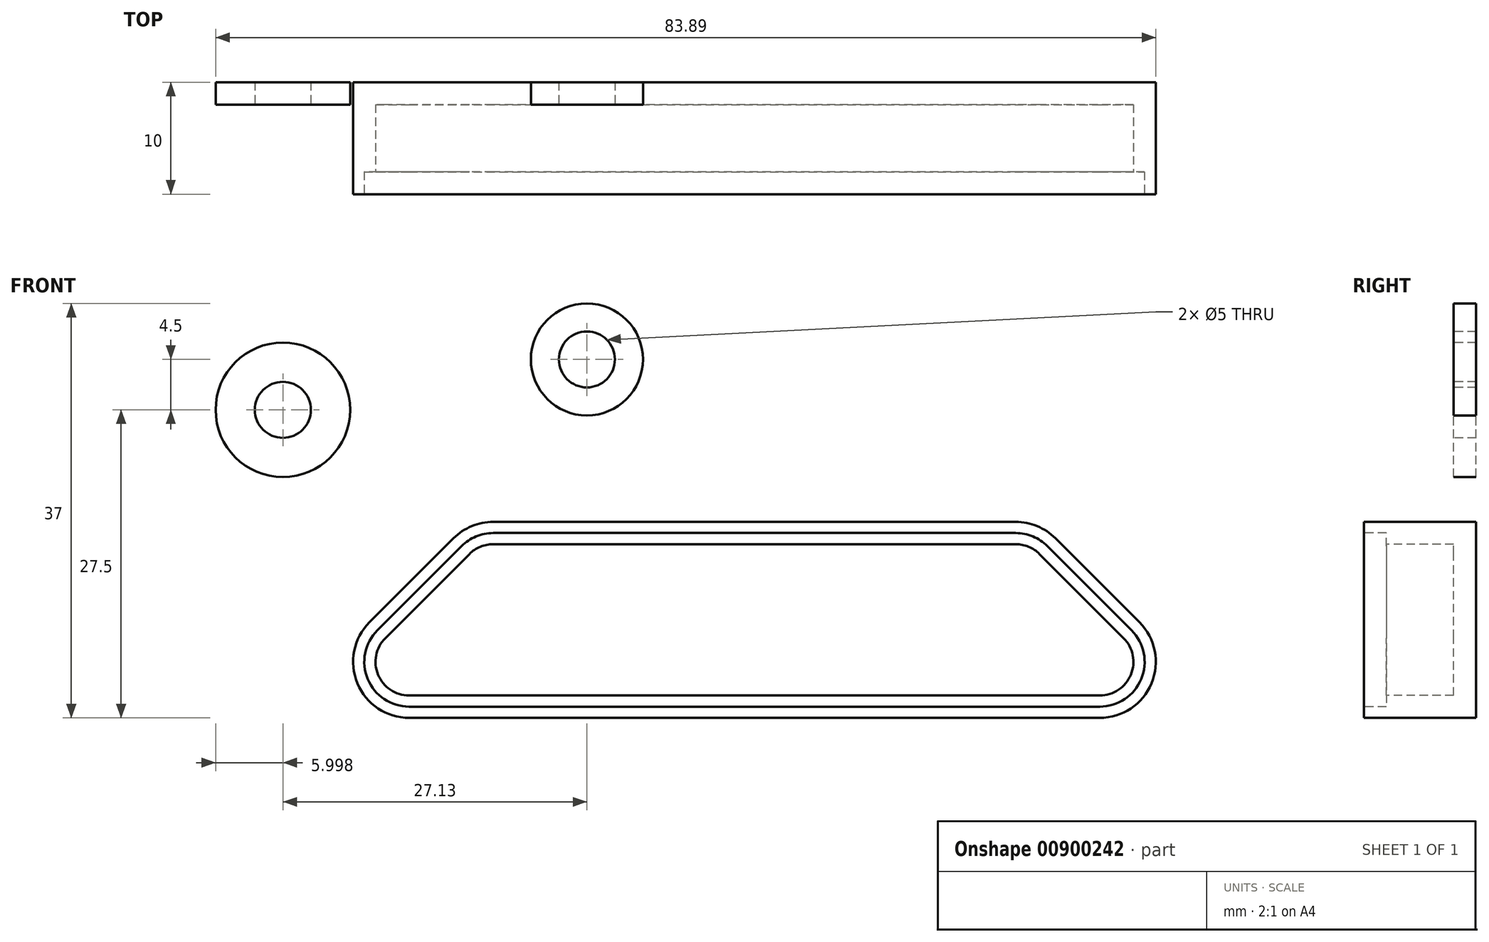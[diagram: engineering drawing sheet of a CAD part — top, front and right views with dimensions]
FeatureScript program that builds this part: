
annotation { "Feature Type Name" : "Feature", "Feature Type Description" : "" }
export const myFeature = defineFeature(function(context is Context, id is Id, definition is map)
    precondition{}
    {
        {
            var Q0;
            Q0=qCreatedBy(makeId("Front.planeOp"),FACE);
            var sketch = newSketch(context, id + "F0", { "sketchPlane" : qUnion([Q0])});
            skLineSegment(sketch, "E0", {"start": v(-36.08, 0) * mm, "end": v(36.08, 0) * mm, "construction": true});
            skArc(sketch, "E1", {"start": v(36.08, -20) * mm, "mid": v(56.08, 0) * mm, "end": v(36.08, 20) * mm});
            skArc(sketch, "E2", {"start": v(-36.08, 20) * mm, "mid": v(-56.08, 0) * mm, "end": v(-36.08, -20) * mm});
            skLineSegment(sketch, "E3", {"start": v(-36.08, 20) * mm, "end": v(36.08, 20) * mm});
            skLineSegment(sketch, "E4.MirrorCS", {"start": v(-36.08, -20) * mm, "end": v(36.08, -20) * mm});
            skSolve(sketch);
        }
        {
            var Q0;
            Q0 = qSketchRegion(id + "F0", true);
            extrude(context, id + "F1", {"entities" : qUnion([Q0]), "depth" : 2 * mm, "offsetDistance" : 25 * mm});
        }
        {
            var Q0;
            Q0=makeQuery(id+"F1.opExtrude","CAP_FACE",FACE,{"disambiguationData":[OSD([sQuery(id+"F0.wireOp",EDGE,"E1"),sQuery(id+"F0.wireOp",EDGE,"E2"),sQuery(id+"F0.wireOp",EDGE,"E3"),sQuery(id+"F0.wireOp",EDGE,"E4.MirrorCS")])],"isStart":false});
            var sketch = newSketch(context, id + "F2", { "sketchPlane" : qUnion([Q0])});
            skLineSegment(sketch, "E5", {"start": v(0, 107.5) * mm, "end": v(0, -106.96) * mm, "construction": true});
            skLineSegment(sketch, "E6", {"start": v(0, -2.5) * mm, "end": v(23.31, -2.5) * mm});
            skLineSegment(sketch, "E7", {"start": v(26.85, -3.96) * mm, "end": v(34.35, -11.46) * mm});
            skLineSegment(sketch, "E8", {"start": v(30.81, -20) * mm, "end": v(0, -20) * mm});
            skArc(sketch, "E9.filletArc", {"start": v(26.85, -3.96) * mm, "mid": v(25.23, -2.88) * mm, "end": v(23.31, -2.5) * mm});
            skArc(sketch, "E10.filletArc", {"start": v(30.81, -20) * mm, "mid": v(35.43, -16.91) * mm, "end": v(34.35, -11.46) * mm});
            skLineSegment(sketch, "E11.MirrorCS", {"start": v(0, -2.5) * mm, "end": v(-23.31, -2.5) * mm});
            skArc(sketch, "E12.MirrorCS", {"start": v(-26.85, -3.96) * mm, "mid": v(-25.23, -2.88) * mm, "end": v(-23.31, -2.5) * mm});
            skLineSegment(sketch, "E13.MirrorCS", {"start": v(-26.85, -3.96) * mm, "end": v(-34.35, -11.46) * mm});
            skArc(sketch, "E14.MirrorCS", {"start": v(-30.81, -20) * mm, "mid": v(-35.43, -16.91) * mm, "end": v(-34.35, -11.46) * mm});
            skLineSegment(sketch, "E15.MirrorCS", {"start": v(-30.81, -20) * mm, "end": v(0, -20) * mm});
            skSolve(sketch);
        }
        {
            var Q0;
            Q0=makeQuery(id+"F2.imprint","IMPRINT",FACE,{"disambiguationData":[TD([[makeQuery(id+"F2.imprint","IMPRINT",EDGE,{"derivedFrom":sQuery(id+"F2.wireOp",EDGE,"E6")}),-1.0]])]});
            var Q1;
            Q1=makeQuery(id+"F2.imprint","IMPRINT",FACE,{"disambiguationData":[TD([[makeQuery(id+"F2.imprint","IMPRINT",EDGE,{"derivedFrom":sQuery(id+"F2.wireOp",EDGE,"1ff64fa8-2fd5-4123-b6a7-406101e30ad4.0")}),1.0]])]});
            var Q2;
            Q2=makeQuery(id+"F2.imprint","IMPRINT",FACE,{"disambiguationData":[TD([[makeQuery(id+"F2.imprint","IMPRINT",EDGE,{"derivedFrom":sQuery(id+"F2.wireOp",EDGE,"6d2cac0a-8418-49f5-aced-8188614ca164.0")}),1.0]])]});
            extrude(context, id + "F3", {"entities" : qUnion([Q0, Q1, Q2]), "operationType" : NewBodyOperationType.ADD, "depth" : 8 * mm, "offsetDistance" : 25 * mm});
        }
        {
            var Q0;
            Q0=makeQuery(id+"F3.opExtrude","CAP_FACE",FACE,{"disambiguationData":[OSD([sQuery(id+"F2.wireOp",EDGE,"E6"),sQuery(id+"F2.wireOp",EDGE,"E7"),sQuery(id+"F2.wireOp",EDGE,"E8"),sQuery(id+"F2.wireOp",EDGE,"E9.filletArc"),sQuery(id+"F2.wireOp",EDGE,"E10.filletArc"),sQuery(id+"F2.wireOp",EDGE,"E11.MirrorCS"),sQuery(id+"F2.wireOp",EDGE,"E12.MirrorCS"),sQuery(id+"F2.wireOp",EDGE,"E13.MirrorCS"),sQuery(id+"F2.wireOp",EDGE,"E14.MirrorCS"),sQuery(id+"F2.wireOp",EDGE,"E15.MirrorCS")])],"isStart":false});
            var sketch = newSketch(context, id + "F4", { "sketchPlane" : qUnion([Q0])});
            skArc(sketch, "E16.0", {"start": v(-33.64, -12.17) * mm, "mid": v(-34.51, -16.53) * mm, "end": v(-30.81, -19) * mm});
            skLineSegment(sketch, "E16.1", {"start": v(-26.14, -4.67) * mm, "end": v(-33.64, -12.17) * mm});
            skLineSegment(sketch, "E16.2", {"start": v(-30.81, -19) * mm, "end": v(30.81, -19) * mm});
            skArc(sketch, "E16.3", {"start": v(-23.31, -3.5) * mm, "mid": v(-24.85, -3.8) * mm, "end": v(-26.14, -4.67) * mm});
            skArc(sketch, "E16.4", {"start": v(30.81, -19) * mm, "mid": v(34.51, -16.53) * mm, "end": v(33.64, -12.17) * mm});
            skLineSegment(sketch, "E16.5", {"start": v(33.64, -12.17) * mm, "end": v(26.14, -4.67) * mm});
            skArc(sketch, "E16.6", {"start": v(26.14, -4.67) * mm, "mid": v(24.85, -3.8) * mm, "end": v(23.31, -3.5) * mm});
            skLineSegment(sketch, "E16.7", {"start": v(23.31, -3.5) * mm, "end": v(-23.31, -3.5) * mm});
            skSolve(sketch);
        }
        {
            var Q0;
            Q0=makeQuery(id+"F4.imprint","IMPRINT",FACE,{"disambiguationData":[TD([[makeQuery(id+"F4.imprint","IMPRINT",EDGE,{"derivedFrom":sQuery(id+"F4.wireOp",EDGE,"E16.0")}),1.0]])]});
            extrude(context, id + "F5", {"entities" : qUnion([Q0]), "operationType" : NewBodyOperationType.REMOVE, "oppositeDirection" : true, "depth" : 2 * mm, "offsetDistance" : 25 * mm});
        }
        {
            var Q0;
            Q0=makeQuery(id+"F5.boolean.opBoolean","COPY",FACE,{"derivedFrom":makeQuery(id+"F5.opExtrude","CAP_FACE",FACE,{"disambiguationData":[OSD([sQuery(id+"F4.wireOp",EDGE,"E16.0"),sQuery(id+"F4.wireOp",EDGE,"E16.1"),sQuery(id+"F4.wireOp",EDGE,"E16.2"),sQuery(id+"F4.wireOp",EDGE,"E16.3"),sQuery(id+"F4.wireOp",EDGE,"E16.4"),sQuery(id+"F4.wireOp",EDGE,"E16.5"),sQuery(id+"F4.wireOp",EDGE,"E16.6"),sQuery(id+"F4.wireOp",EDGE,"E16.7")])],"isStart":false})});
            var sketch = newSketch(context, id + "F6", { "sketchPlane" : qUnion([Q0])});
            skLineSegment(sketch, "E17.0", {"start": v(32.94, -12.88) * mm, "end": v(25.44, -5.38) * mm});
            skArc(sketch, "E17.1", {"start": v(30.81, -18) * mm, "mid": v(33.59, -16.15) * mm, "end": v(32.94, -12.88) * mm});
            skArc(sketch, "E17.2", {"start": v(25.44, -5.38) * mm, "mid": v(24.46, -4.73) * mm, "end": v(23.31, -4.5) * mm});
            skLineSegment(sketch, "E17.3", {"start": v(-30.81, -18) * mm, "end": v(30.81, -18) * mm});
            skLineSegment(sketch, "E17.4", {"start": v(23.31, -4.5) * mm, "end": v(-23.31, -4.5) * mm});
            skArc(sketch, "E17.5", {"start": v(-23.31, -4.5) * mm, "mid": v(-24.46, -4.73) * mm, "end": v(-25.44, -5.38) * mm});
            skLineSegment(sketch, "E17.6", {"start": v(-25.44, -5.38) * mm, "end": v(-32.94, -12.88) * mm});
            skArc(sketch, "E17.7", {"start": v(-32.94, -12.88) * mm, "mid": v(-33.59, -16.15) * mm, "end": v(-30.81, -18) * mm});
            skSolve(sketch);
        }
        {
            var Q0;
            Q0=makeQuery(id+"F6.imprint","IMPRINT",FACE,{"disambiguationData":[TD([[makeQuery(id+"F6.imprint","IMPRINT",EDGE,{"derivedFrom":sQuery(id+"F6.wireOp",EDGE,"E17.0")}),1.0]])]});
            extrude(context, id + "F7", {"entities" : qUnion([Q0]), "operationType" : NewBodyOperationType.REMOVE, "oppositeDirection" : true, "depth" : 6 * mm, "offsetDistance" : 25 * mm});
        }
        {
            var Q0;
            Q0=makeQuery(id+"F1.opExtrude","CAP_FACE",FACE,{"disambiguationData":[OSD([sQuery(id+"F0.wireOp",EDGE,"E1"),sQuery(id+"F0.wireOp",EDGE,"E2"),sQuery(id+"F0.wireOp",EDGE,"E3"),sQuery(id+"F0.wireOp",EDGE,"E4.MirrorCS")])],"isStart":false});
            var sketch = newSketch(context, id + "F8", { "sketchPlane" : qUnion([Q0])});
            skCircle(sketch, "E18", {"center": v(42.08, 7.5) * mm, "radius": 6 * mm});
            skLineSegment(sketch, "E19", {"start": v(61.14, 0) * mm, "end": v(-61.86, 0) * mm, "construction": true});
            skLineSegment(sketch, "E20", {"start": v(0, 29.23) * mm, "end": v(0, -29.55) * mm, "construction": true});
            skCircle(sketch, "E21", {"center": v(14.95, 12) * mm, "radius": 5 * mm});
            skCircle(sketch, "E22.MirrorC", {"center": v(-42.08, 7.5) * mm, "radius": 6 * mm});
            skCircle(sketch, "E23.MirrorC", {"center": v(-14.95, 12) * mm, "radius": 5 * mm});
            skSolve(sketch);
        }
        {
            var Q0;
            Q0=makeQuery(id+"F8.imprint","IMPRINT",FACE,{"disambiguationData":[TD([[makeQuery(id+"F8.imprint","IMPRINT",EDGE,{"derivedFrom":sQuery(id+"F8.wireOp",EDGE,"E23.MirrorC")}),-1.0]])]});
            var Q1;
            Q1=makeQuery(id+"F8.imprint","IMPRINT",FACE,{"disambiguationData":[TD([[makeQuery(id+"F8.imprint","IMPRINT",EDGE,{"derivedFrom":sQuery(id+"F8.wireOp",EDGE,"E22.MirrorC")}),-1.0]])]});
            var Q2;
            Q2=makeQuery(id+"F8.imprint","IMPRINT",FACE,{"disambiguationData":[TD([[makeQuery(id+"F8.imprint","IMPRINT",EDGE,{"derivedFrom":sQuery(id+"F8.wireOp",EDGE,"E21")}),1.0]])]});
            var Q3;
            Q3=makeQuery(id+"F8.imprint","IMPRINT",FACE,{"disambiguationData":[TD([[makeQuery(id+"F8.imprint","IMPRINT",EDGE,{"derivedFrom":sQuery(id+"F8.wireOp",EDGE,"E18")}),1.0]])]});
            extrude(context, id + "F9", {"entities" : qUnion([Q0, Q1, Q2, Q3]), "operationType" : NewBodyOperationType.ADD, "depth" : 1 * mm, "offsetDistance" : 25 * mm});
        }
        {
            var Q0;
            Q0=makeQuery(id+"F9.opExtrude","CAP_FACE",FACE,{"disambiguationData":[OSD([sQuery(id+"F8.wireOp",EDGE,"E23.MirrorC")])],"isStart":false});
            var sketch = newSketch(context, id + "F10", { "sketchPlane" : qUnion([Q0])});
            skCircle(sketch, "E24", {"center": v(-14.95, 12) * mm, "radius": 2.5 * mm});
            skLineSegment(sketch, "E25", {"start": v(0, 25.65) * mm, "end": v(0, -22.35) * mm, "construction": true});
            skCircle(sketch, "E26.MirrorC", {"center": v(14.95, 12) * mm, "radius": 2.5 * mm});
            skSolve(sketch);
        }
        {
            var Q0;
            Q0=makeQuery(id+"F9.opExtrude","CAP_FACE",FACE,{"disambiguationData":[OSD([sQuery(id+"F8.wireOp",EDGE,"E22.MirrorC")])],"isStart":false});
            var sketch = newSketch(context, id + "F11", { "sketchPlane" : qUnion([Q0])});
            skCircle(sketch, "E27", {"center": v(-42.08, 7.5) * mm, "radius": 2.5 * mm});
            skLineSegment(sketch, "E28", {"start": v(0, 25.47) * mm, "end": v(0, -27.42) * mm, "construction": true});
            skCircle(sketch, "E29.MirrorC", {"center": v(42.08, 7.5) * mm, "radius": 2.5 * mm});
            skSolve(sketch);
        }
        {
            var Q0;
            Q0=makeQuery(id+"F10.imprint","IMPRINT",FACE,{"disambiguationData":[TD([[makeQuery(id+"F10.imprint","IMPRINT",EDGE,{"derivedFrom":sQuery(id+"F10.wireOp",EDGE,"E24")}),1.0]])]});
            var Q1;
            Q1=makeQuery(id+"F11.imprint","IMPRINT",FACE,{"disambiguationData":[TD([[makeQuery(id+"F11.imprint","IMPRINT",EDGE,{"derivedFrom":sQuery(id+"F11.wireOp",EDGE,"E27")}),1.0]])]});
            var Q2;
            Q2=makeQuery(id+"F10.imprint","IMPRINT",FACE,{"disambiguationData":[TD([[makeQuery(id+"F10.imprint","IMPRINT",EDGE,{"derivedFrom":sQuery(id+"F10.wireOp",EDGE,"E26.MirrorC")}),-1.0]])]});
            var Q3;
            Q3=makeQuery(id+"F11.imprint","IMPRINT",FACE,{"disambiguationData":[TD([[makeQuery(id+"F11.imprint","IMPRINT",EDGE,{"derivedFrom":sQuery(id+"F11.wireOp",EDGE,"E29.MirrorC")}),-1.0]])]});
            extrude(context, id + "F12", {"entities" : qUnion([Q0, Q1, Q2, Q3]), "operationType" : NewBodyOperationType.REMOVE, "endBound" : BoundingType.THROUGH_ALL, "oppositeDirection" : true, "depth" : 25 * mm, "offsetDistance" : 25 * mm});
        }
    });
